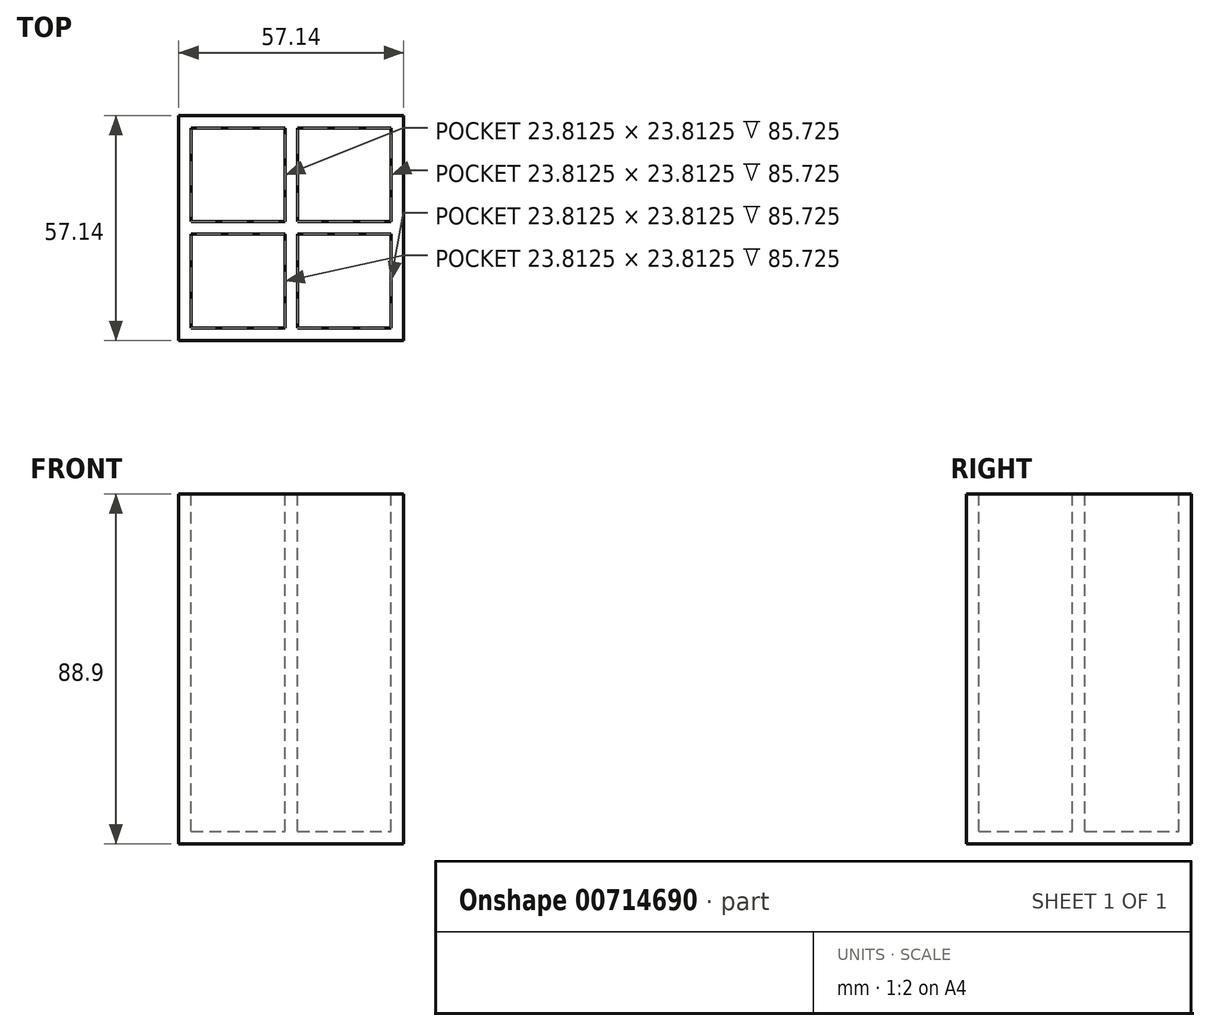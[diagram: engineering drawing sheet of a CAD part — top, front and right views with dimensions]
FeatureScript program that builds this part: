
annotation { "Feature Type Name" : "Feature", "Feature Type Description" : "" }
export const myFeature = defineFeature(function(context is Context, id is Id, definition is map)
    precondition{}
    {
        {
            var Q0;
            Q0=qCreatedBy(makeId("Top.planeOp"),FACE);
            var sketch = newSketch(context, id + "F0", { "sketchPlane" : qUnion([Q0])});
            skLineSegment(sketch, "E0.bottom", {"start": v(-28.57, -28.58) * mm, "end": v(28.58, -28.58) * mm});
            skLineSegment(sketch, "E0.top", {"start": v(-28.58, 28.58) * mm, "end": v(28.57, 28.58) * mm});
            skLineSegment(sketch, "E0.left", {"start": v(-28.57, -28.58) * mm, "end": v(-28.58, 28.58) * mm});
            skLineSegment(sketch, "E0.right", {"start": v(28.58, -28.58) * mm, "end": v(28.57, 28.58) * mm});
            skPoint(sketch, "E0.middle", {"position": v(0, 0) * mm});
            skSolve(sketch);
        }
        {
            var Q0;
            Q0 = qSketchRegion(id + "F0", true);
            extrude(context, id + "F1", {"entities" : qUnion([Q0]), "depth" : 88.9 * mm, "offsetDistance" : 25.4 * mm});
        }
        {
            var Q0;
            Q0=makeQuery(id+"F1.opExtrude","CAP_FACE",FACE,{"disambiguationData":[OSD([sQuery(id+"F0.wireOp",EDGE,"E0.bottom"),sQuery(id+"F0.wireOp",EDGE,"E0.top"),sQuery(id+"F0.wireOp",EDGE,"E0.left"),sQuery(id+"F0.wireOp",EDGE,"E0.right")])],"isStart":false});
            var sketch = newSketch(context, id + "F2", { "sketchPlane" : qUnion([Q0])});
            skLineSegment(sketch, "E1", {"start": v(0, 28.58) * mm, "end": v(0, -28.58) * mm});
            skLineSegment(sketch, "E2", {"start": v(-28.58, 0) * mm, "end": v(28.58, 0) * mm});
            skLineSegment(sketch, "E3", {"start": v(-28.58, 1.59) * mm, "end": v(28.58, 1.59) * mm});
            skLineSegment(sketch, "E4", {"start": v(-28.58, -1.59) * mm, "end": v(28.58, -1.59) * mm});
            skLineSegment(sketch, "E5", {"start": v(-28.58, 25.4) * mm, "end": v(28.58, 25.4) * mm});
            skLineSegment(sketch, "E6", {"start": v(-28.57, -25.4) * mm, "end": v(28.58, -25.4) * mm});
            skLineSegment(sketch, "E7", {"start": v(-25.4, -28.58) * mm, "end": v(-25.4, 28.58) * mm});
            skLineSegment(sketch, "E8", {"start": v(25.4, -28.58) * mm, "end": v(25.4, 28.58) * mm});
            skLineSegment(sketch, "E9", {"start": v(-1.59, 28.58) * mm, "end": v(-1.59, -28.58) * mm});
            skLineSegment(sketch, "E10", {"start": v(1.59, -28.58) * mm, "end": v(1.59, 28.58) * mm});
            skSolve(sketch);
        }
        {
            var Q0;
            {var subQ0=sQuery(id+"F2.wireOp",EDGE,"E7");var subQ1=sQuery(id+"F2.wireOp",EDGE,"E3");var subQ2=makeQuery(id+"F2.imprint","INTERSECT",VERTEX,{"derivedFrom":[subQ1,subQ0]});Q0=makeQuery(id+"F2.imprint","IMPRINT",FACE,{"disambiguationData":[TD([[makeQuery(id+"F2.imprint","IMPRINT",EDGE,{"disambiguationData":[TD([[subQ2,-1.0]])],"derivedFrom":subQ1}),1.0]])]});}
            var Q1;
            {var subQ0=sQuery(id+"F2.wireOp",EDGE,"E10");var subQ1=sQuery(id+"F2.wireOp",EDGE,"E3");var subQ2=makeQuery(id+"F2.imprint","INTERSECT",VERTEX,{"derivedFrom":[subQ1,subQ0]});Q1=makeQuery(id+"F2.imprint","IMPRINT",FACE,{"disambiguationData":[TD([[makeQuery(id+"F2.imprint","IMPRINT",EDGE,{"disambiguationData":[TD([[subQ2,-1.0]])],"derivedFrom":subQ1}),1.0]])]});}
            var Q2;
            {var subQ0=sQuery(id+"F2.wireOp",EDGE,"E10");var subQ1=sQuery(id+"F2.wireOp",EDGE,"E4");var subQ2=makeQuery(id+"F2.imprint","INTERSECT",VERTEX,{"derivedFrom":[subQ1,subQ0]});Q2=makeQuery(id+"F2.imprint","IMPRINT",FACE,{"disambiguationData":[TD([[makeQuery(id+"F2.imprint","IMPRINT",EDGE,{"disambiguationData":[TD([[subQ2,-1.0]])],"derivedFrom":subQ1}),-1.0]])]});}
            var Q3;
            {var subQ0=sQuery(id+"F2.wireOp",EDGE,"E7");var subQ1=sQuery(id+"F2.wireOp",EDGE,"E4");var subQ2=makeQuery(id+"F2.imprint","INTERSECT",VERTEX,{"derivedFrom":[subQ1,subQ0]});Q3=makeQuery(id+"F2.imprint","IMPRINT",FACE,{"disambiguationData":[TD([[makeQuery(id+"F2.imprint","IMPRINT",EDGE,{"disambiguationData":[TD([[subQ2,-1.0]])],"derivedFrom":subQ1}),-1.0]])]});}
            extrude(context, id + "F3", {"entities" : qUnion([Q0, Q1, Q2, Q3]), "operationType" : NewBodyOperationType.REMOVE, "oppositeDirection" : true, "depth" : 85.72 * mm, "offsetDistance" : 25.4 * mm});
        }
    });
